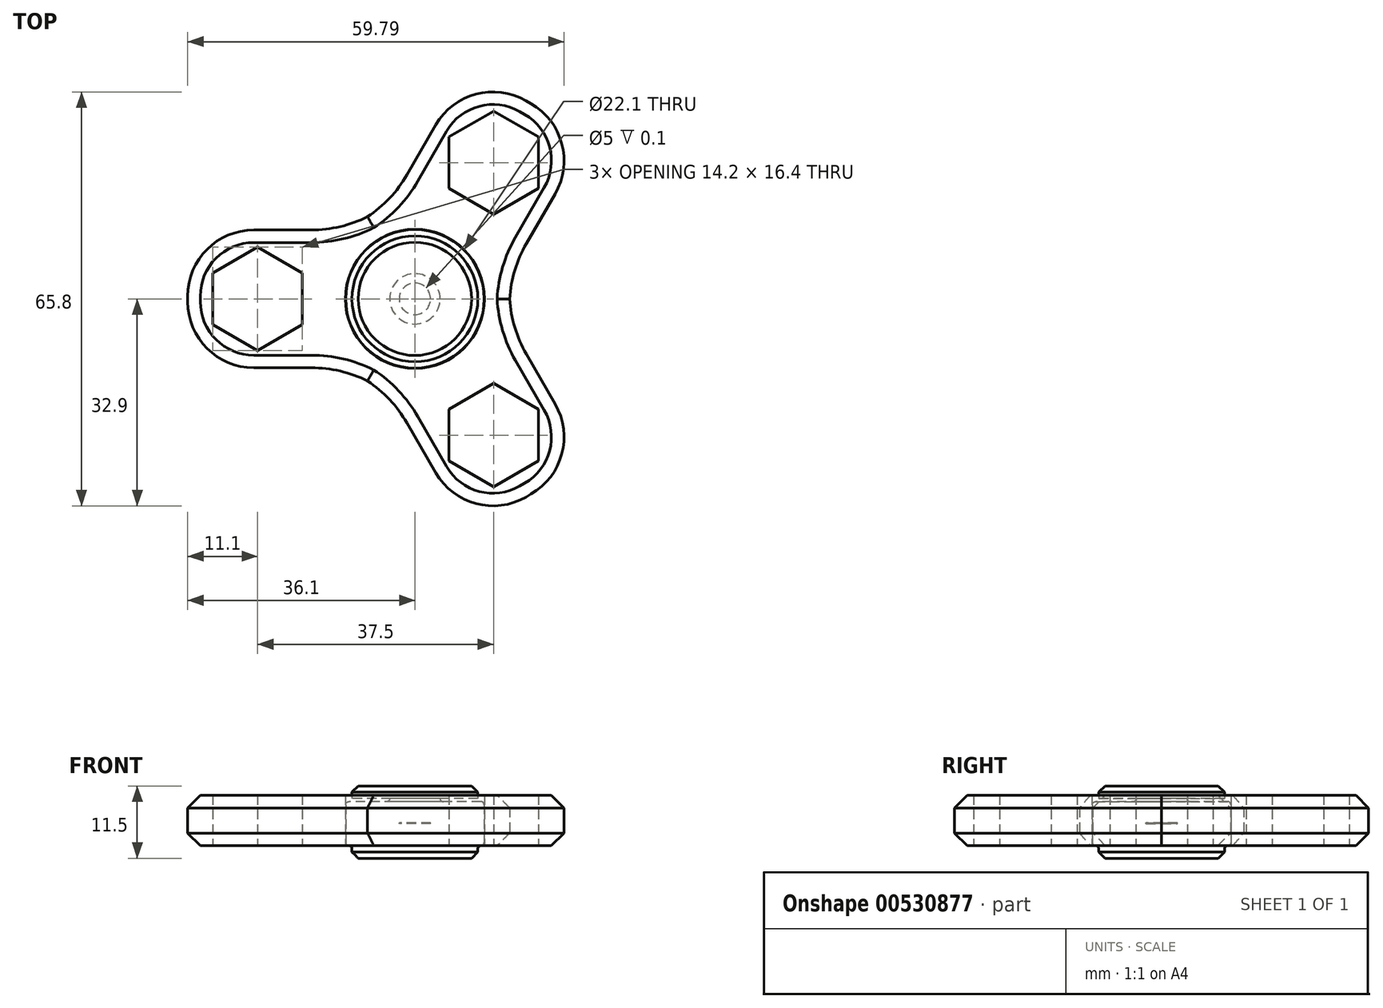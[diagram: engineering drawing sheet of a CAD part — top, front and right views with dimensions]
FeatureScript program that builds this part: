
annotation { "Feature Type Name" : "Feature", "Feature Type Description" : "" }
export const myFeature = defineFeature(function(context is Context, id is Id, definition is map)
    precondition{}
    {
        {
            var Q0;
            Q0=qCreatedBy(makeId("Top.planeOp"),FACE);
            var sketch = newSketch(context, id + "F0", { "sketchPlane" : qUnion([Q0])});
            skCircle(sketch, "E0", {"center": v(0, 0) * mm, "radius": 11 * mm});
            skCircle(sketch, "E1", {"center": v(0, 0) * mm, "radius": 4 * mm});
            skSolve(sketch);
        }
        {
            var Q0;
            Q0=makeQuery(id+"F0.imprint","IMPRINT",FACE,{"disambiguationData":[TD([[makeQuery(id+"F0.imprint","IMPRINT",EDGE,{"derivedFrom":sQuery(id+"F0.wireOp",EDGE,"E0")}),1.0]])]});
            extrude(context, id + "F1", {"entities" : qUnion([Q0]), "depth" : 7 * mm, "offsetDistance" : 25 * mm});
        }
        {
            var Q0;
            Q0=makeQuery(id+"F1.opExtrude","CAP_FACE",FACE,{"disambiguationData":[OSD([sQuery(id+"F0.wireOp",EDGE,"E0"),sQuery(id+"F0.wireOp",EDGE,"E1")])],"isStart":true});
            var sketch = newSketch(context, id + "F2", { "sketchPlane" : qUnion([Q0])});
            skCircle(sketch, "E2.0", {"center": v(0, 0) * mm, "radius": 11.05 * mm});
            skCircle(sketch, "E3.0", {"center": v(0, 0) * mm, "radius": 15.05 * mm});
            skLineSegment(sketch, "E4", {"start": v(0, 0) * mm, "end": v(-25, 0) * mm, "construction": true});
            skPoint(sketch, "E5.middle", {"position": v(-25, 0) * mm});
            skCircle(sketch, "E6", {"center": v(0, 0) * mm, "radius": 50 * mm, "construction": true});
            skCircle(sketch, "E7", {"center": v(-25, 0) * mm, "radius": 8.2 * mm, "construction": true});
            skLineSegment(sketch, "E8.0", {"start": v(-25, -8.2) * mm, "end": v(-32.1, -4.1) * mm});
            skLineSegment(sketch, "E8.1", {"start": v(-32.1, -4.1) * mm, "end": v(-32.1, 4.1) * mm});
            skLineSegment(sketch, "E8.2", {"start": v(-32.1, 4.1) * mm, "end": v(-25, 8.2) * mm});
            skLineSegment(sketch, "E8.3", {"start": v(-25, 8.2) * mm, "end": v(-17.9, 4.1) * mm});
            skLineSegment(sketch, "E8.4", {"start": v(-17.9, 4.1) * mm, "end": v(-17.9, -4.1) * mm});
            skLineSegment(sketch, "E8.5", {"start": v(-17.9, -4.1) * mm, "end": v(-25, -8.2) * mm});
            skLineSegment(sketch, "E9", {"start": v(0, -8.2) * mm, "end": v(-34.67, -8.2) * mm, "construction": true});
            skLineSegment(sketch, "E10", {"start": v(0, 8.2) * mm, "end": v(-34.67, 8.2) * mm, "construction": true});
            skLineSegment(sketch, "E11.0", {"start": v(-1.48, 10.95) * mm, "end": v(-6, 10.95) * mm, "construction": true});
            skLineSegment(sketch, "E12.0", {"start": v(-1.48, -10.95) * mm, "end": v(-6, -10.95) * mm, "construction": true});
            skLineSegment(sketch, "E13", {"start": v(-36.1, -0.45) * mm, "end": v(-36.1, 0.45) * mm});
            skLineSegment(sketch, "E14", {"start": v(-25, 0) * mm, "end": v(-36.1, 0) * mm, "construction": true});
            skPoint(sketch, "E15.visualSharp", {"position": v(-36.1, -10.95) * mm});
            skArc(sketch, "E15.filletArc", {"start": v(-36.1, -0.45) * mm, "mid": v(-33.03, -7.87) * mm, "end": v(-25.6, -10.95) * mm});
            skPoint(sketch, "E16.visualSharp", {"position": v(-36.1, 10.95) * mm});
            skArc(sketch, "E16.filletArc", {"start": v(-25.6, 10.95) * mm, "mid": v(-33.03, 7.87) * mm, "end": v(-36.1, 0.45) * mm});
            skLineSegment(sketch, "E17.trimOffspring", {"start": v(-10.32, -10.95) * mm, "end": v(-25.6, -10.95) * mm});
            skLineSegment(sketch, "E18.trimOffspring", {"start": v(-10.32, 10.95) * mm, "end": v(-25.6, 10.95) * mm});
            skLineSegment(sketch, "E19.1.0", {"start": v(12.5, -13.45) * mm, "end": v(19.6, -17.55) * mm});
            skLineSegment(sketch, "E19.1.1", {"start": v(5.4, -17.55) * mm, "end": v(12.5, -13.45) * mm});
            skLineSegment(sketch, "E19.1.2", {"start": v(5.4, -25.75) * mm, "end": v(5.4, -17.55) * mm});
            skLineSegment(sketch, "E19.1.3", {"start": v(12.5, -29.85) * mm, "end": v(5.4, -25.75) * mm});
            skLineSegment(sketch, "E19.1.4", {"start": v(19.6, -25.75) * mm, "end": v(12.5, -29.85) * mm});
            skLineSegment(sketch, "E19.1.5", {"start": v(19.6, -17.55) * mm, "end": v(19.6, -25.75) * mm});
            skArc(sketch, "E19.1.6", {"start": v(18.44, -31.04) * mm, "mid": v(23.33, -24.66) * mm, "end": v(22.28, -16.7) * mm});
            skLineSegment(sketch, "E19.1.7", {"start": v(14.65, -3.47) * mm, "end": v(22.28, -16.7) * mm});
            skLineSegment(sketch, "E19.1.8", {"start": v(-4.32, -14.42) * mm, "end": v(3.32, -27.65) * mm});
            skArc(sketch, "E19.1.9", {"start": v(3.32, -27.65) * mm, "mid": v(9.7, -32.54) * mm, "end": v(17.66, -31.49) * mm});
            skLineSegment(sketch, "E19.1.10", {"start": v(18.44, -31.04) * mm, "end": v(17.66, -31.49) * mm});
            skLineSegment(sketch, "E19.2.0", {"start": v(5.4, 17.55) * mm, "end": v(5.4, 25.75) * mm});
            skLineSegment(sketch, "E19.2.1", {"start": v(12.5, 13.45) * mm, "end": v(5.4, 17.55) * mm});
            skLineSegment(sketch, "E19.2.2", {"start": v(19.6, 17.55) * mm, "end": v(12.5, 13.45) * mm});
            skLineSegment(sketch, "E19.2.3", {"start": v(19.6, 25.75) * mm, "end": v(19.6, 17.55) * mm});
            skLineSegment(sketch, "E19.2.4", {"start": v(12.5, 29.85) * mm, "end": v(19.6, 25.75) * mm});
            skLineSegment(sketch, "E19.2.5", {"start": v(5.4, 25.75) * mm, "end": v(12.5, 29.85) * mm});
            skArc(sketch, "E19.2.6", {"start": v(17.66, 31.49) * mm, "mid": v(9.7, 32.54) * mm, "end": v(3.32, 27.65) * mm});
            skLineSegment(sketch, "E19.2.7", {"start": v(-4.32, 14.42) * mm, "end": v(3.32, 27.65) * mm});
            skLineSegment(sketch, "E19.2.8", {"start": v(14.65, 3.47) * mm, "end": v(22.28, 16.7) * mm});
            skArc(sketch, "E19.2.9", {"start": v(22.28, 16.7) * mm, "mid": v(23.33, 24.66) * mm, "end": v(18.44, 31.04) * mm});
            skLineSegment(sketch, "E19.2.10", {"start": v(17.66, 31.49) * mm, "end": v(18.44, 31.04) * mm});
            skSolve(sketch);
        }
        {
            var Q0;
            {var subQ5=sQuery(id+"F2.wireOp",EDGE,"2090168d-b076-447e-ab9d-785cbba13f1d.2.0");Q0=makeQuery(id+"F2.imprint","IMPRINT",FACE,{"disambiguationData":[TD([[makeQuery(id+"F2.imprint","IMPRINT",EDGE,{"derivedFrom":subQ5}),-1.0]])]});}
            var Q1;
            Q1=makeQuery(id+"F2.imprint","IMPRINT",FACE,{"disambiguationData":[TD([[makeQuery(id+"F2.imprint","IMPRINT",EDGE,{"derivedFrom":sQuery(id+"F2.wireOp",EDGE,"E2.0")}),-1.0]])]});
            var Q2;
            {var subQ6=sQuery(id+"F2.wireOp",EDGE,"2090168d-b076-447e-ab9d-785cbba13f1d.1.0");Q2=makeQuery(id+"F2.imprint","IMPRINT",FACE,{"disambiguationData":[TD([[makeQuery(id+"F2.imprint","IMPRINT",EDGE,{"derivedFrom":subQ6}),-1.0]])]});}
            var Q3;
            {var subQ5=sQuery(id+"F2.wireOp",EDGE,"E5.bottom");Q3=makeQuery(id+"F2.imprint","IMPRINT",FACE,{"disambiguationData":[TD([[makeQuery(id+"F2.imprint","IMPRINT",EDGE,{"derivedFrom":subQ5}),-1.0]])]});}
            var Q4;
            {var subQ3=sQuery(id+"F2.wireOp",EDGE,"E8.0");Q4=makeQuery(id+"F2.imprint","IMPRINT",FACE,{"disambiguationData":[TD([[makeQuery(id+"F2.imprint","IMPRINT",EDGE,{"derivedFrom":subQ3}),1.0]])]});}
            var Q5;
            {var subQ7=sQuery(id+"F2.wireOp",EDGE,"1de061e3-998c-4d38-ad47-f643a90dabba.1.3");Q5=makeQuery(id+"F2.imprint","IMPRINT",FACE,{"disambiguationData":[TD([[makeQuery(id+"F2.imprint","IMPRINT",EDGE,{"derivedFrom":subQ7}),1.0]])]});}
            var Q6;
            {var subQ5=sQuery(id+"F2.wireOp",EDGE,"1de061e3-998c-4d38-ad47-f643a90dabba.2.3");Q6=makeQuery(id+"F2.imprint","IMPRINT",FACE,{"disambiguationData":[TD([[makeQuery(id+"F2.imprint","IMPRINT",EDGE,{"derivedFrom":subQ5}),1.0]])]});}
            var Q7;
            {var subQ6=sQuery(id+"F2.wireOp",EDGE,"E19.2.3");Q7=makeQuery(id+"F2.imprint","IMPRINT",FACE,{"disambiguationData":[TD([[makeQuery(id+"F2.imprint","IMPRINT",EDGE,{"derivedFrom":subQ6}),1.0]])]});}
            var Q8;
            {var subQ7=sQuery(id+"F2.wireOp",EDGE,"E19.1.3");Q8=makeQuery(id+"F2.imprint","IMPRINT",FACE,{"disambiguationData":[TD([[makeQuery(id+"F2.imprint","IMPRINT",EDGE,{"derivedFrom":subQ7}),1.0]])]});}
            extrude(context, id + "F3", {"entities" : qUnion([Q0, Q1, Q2, Q3, Q4, Q5, Q6, Q7, Q8]), "oppositeDirection" : true, "depth" : 8 * mm, "offsetDistance" : 25 * mm});
        }
        {
            var Q0;
            Q0=makeQuery(id+"F3.opExtrude","SWEPT_EDGE",EDGE,{"disambiguationData":[OSD([sQuery(id+"F2.wireOp",EDGE,"E3.0"),sQuery(id+"F2.wireOp",EDGE,"2090168d-b076-447e-ab9d-785cbba13f1d.2.3")])]});
            var Q1;
            Q1=makeQuery(id+"F3.opExtrude","SWEPT_EDGE",EDGE,{"disambiguationData":[OSD([sQuery(id+"F2.wireOp",EDGE,"E3.0"),sQuery(id+"F2.wireOp",EDGE,"2090168d-b076-447e-ab9d-785cbba13f1d.1.8")])]});
            var Q2;
            Q2=makeQuery(id+"F3.opExtrude","SWEPT_EDGE",EDGE,{"disambiguationData":[OSD([sQuery(id+"F2.wireOp",EDGE,"E3.0"),sQuery(id+"F2.wireOp",EDGE,"2090168d-b076-447e-ab9d-785cbba13f1d.2.8")])]});
            var Q3;
            Q3=makeQuery(id+"F3.opExtrude","SWEPT_EDGE",EDGE,{"disambiguationData":[OSD([sQuery(id+"F2.wireOp",EDGE,"E3.0"),sQuery(id+"F2.wireOp",EDGE,"7743fc66-aecd-449a-ba36-aedd3b808c0c.trimOffspring")])]});
            var Q4;
            Q4=makeQuery(id+"F3.opExtrude","SWEPT_EDGE",EDGE,{"disambiguationData":[OSD([sQuery(id+"F2.wireOp",EDGE,"E3.0"),sQuery(id+"F2.wireOp",EDGE,"1c2b6c41-6d39-4d1e-a6ba-ca666f8f76650.MirrorCS")])]});
            var Q5;
            Q5=makeQuery(id+"F3.opExtrude","SWEPT_EDGE",EDGE,{"disambiguationData":[OSD([sQuery(id+"F2.wireOp",EDGE,"E3.0"),sQuery(id+"F2.wireOp",EDGE,"2090168d-b076-447e-ab9d-785cbba13f1d.1.3")])]});
            fillet(context, id + "F4", {"entities" : qUnion([Q0, Q1, Q2, Q3, Q4, Q5]), "radius" : 20 * mm, "tangentPropagation" : true, "allowEdgeOverflow" : false});
        }
        {
            var Q0;
            Q0=makeQuery(id+"F3.opExtrude","CAP_EDGE",EDGE,{"disambiguationData":[OSD([sQuery(id+"F2.wireOp",EDGE,"E19.2.9")])],"isStart":false});
            var Q1;
            {var subQ0=sQuery(id+"F2.wireOp",EDGE,"E17.trimOffspring");var subQ1=sQuery(id+"F2.wireOp",EDGE,"E3.0");Q1=makeQuery(id+"F4.opFillet","BLEND_EDGE",EDGE,{"blendedFrom":[makeQuery(id+"F3.opExtrude","SWEPT_EDGE",EDGE,{"disambiguationData":[OSD([subQ1,subQ0])]}),makeQuery(id+"F3.opExtrude","CAP_FACE",FACE,{"disambiguationData":[OSD([sQuery(id+"F2.wireOp",EDGE,"E2.0"),subQ1,sQuery(id+"F2.wireOp",EDGE,"E8.0"),sQuery(id+"F2.wireOp",EDGE,"E8.1"),sQuery(id+"F2.wireOp",EDGE,"E8.2"),sQuery(id+"F2.wireOp",EDGE,"E8.3"),sQuery(id+"F2.wireOp",EDGE,"E8.4"),sQuery(id+"F2.wireOp",EDGE,"E8.5"),sQuery(id+"F2.wireOp",EDGE,"E15.filletArc"),sQuery(id+"F2.wireOp",EDGE,"E16.filletArc"),subQ0,sQuery(id+"F2.wireOp",EDGE,"E18.trimOffspring"),sQuery(id+"F2.wireOp",EDGE,"E19.1.0"),sQuery(id+"F2.wireOp",EDGE,"E19.1.1"),sQuery(id+"F2.wireOp",EDGE,"E19.1.2"),sQuery(id+"F2.wireOp",EDGE,"E19.1.3"),sQuery(id+"F2.wireOp",EDGE,"E19.1.4"),sQuery(id+"F2.wireOp",EDGE,"E19.1.5"),sQuery(id+"F2.wireOp",EDGE,"E19.1.6"),sQuery(id+"F2.wireOp",EDGE,"E19.1.7"),sQuery(id+"F2.wireOp",EDGE,"E19.1.8"),sQuery(id+"F2.wireOp",EDGE,"E19.1.9"),sQuery(id+"F2.wireOp",EDGE,"E19.2.0"),sQuery(id+"F2.wireOp",EDGE,"E19.2.1"),sQuery(id+"F2.wireOp",EDGE,"E19.2.2"),sQuery(id+"F2.wireOp",EDGE,"E19.2.3"),sQuery(id+"F2.wireOp",EDGE,"E19.2.4"),sQuery(id+"F2.wireOp",EDGE,"E19.2.5"),sQuery(id+"F2.wireOp",EDGE,"E19.2.6"),sQuery(id+"F2.wireOp",EDGE,"E19.2.7"),sQuery(id+"F2.wireOp",EDGE,"E19.2.8"),sQuery(id+"F2.wireOp",EDGE,"E19.2.9")])],"isStart":false})],"blendedInto":[makeQuery(id+"F3.opExtrude","CAP_FACE",FACE,{"disambiguationData":[OSD([sQuery(id+"F2.wireOp",EDGE,"E2.0"),subQ1,sQuery(id+"F2.wireOp",EDGE,"E8.0"),sQuery(id+"F2.wireOp",EDGE,"E8.1"),sQuery(id+"F2.wireOp",EDGE,"E8.2"),sQuery(id+"F2.wireOp",EDGE,"E8.3"),sQuery(id+"F2.wireOp",EDGE,"E8.4"),sQuery(id+"F2.wireOp",EDGE,"E8.5"),sQuery(id+"F2.wireOp",EDGE,"E15.filletArc"),sQuery(id+"F2.wireOp",EDGE,"E16.filletArc"),subQ0,sQuery(id+"F2.wireOp",EDGE,"E18.trimOffspring"),sQuery(id+"F2.wireOp",EDGE,"E19.1.0"),sQuery(id+"F2.wireOp",EDGE,"E19.1.1"),sQuery(id+"F2.wireOp",EDGE,"E19.1.2"),sQuery(id+"F2.wireOp",EDGE,"E19.1.3"),sQuery(id+"F2.wireOp",EDGE,"E19.1.4"),sQuery(id+"F2.wireOp",EDGE,"E19.1.5"),sQuery(id+"F2.wireOp",EDGE,"E19.1.6"),sQuery(id+"F2.wireOp",EDGE,"E19.1.7"),sQuery(id+"F2.wireOp",EDGE,"E19.1.8"),sQuery(id+"F2.wireOp",EDGE,"E19.1.9"),sQuery(id+"F2.wireOp",EDGE,"E19.2.0"),sQuery(id+"F2.wireOp",EDGE,"E19.2.1"),sQuery(id+"F2.wireOp",EDGE,"E19.2.2"),sQuery(id+"F2.wireOp",EDGE,"E19.2.3"),sQuery(id+"F2.wireOp",EDGE,"E19.2.4"),sQuery(id+"F2.wireOp",EDGE,"E19.2.5"),sQuery(id+"F2.wireOp",EDGE,"E19.2.6"),sQuery(id+"F2.wireOp",EDGE,"E19.2.7"),sQuery(id+"F2.wireOp",EDGE,"E19.2.8"),sQuery(id+"F2.wireOp",EDGE,"E19.2.9")])],"isStart":false})]});}
            var Q2;
            Q2=makeQuery(id+"F3.opExtrude","CAP_EDGE",EDGE,{"disambiguationData":[OSD([sQuery(id+"F2.wireOp",EDGE,"E19.1.6")])],"isStart":false});
            var Q3;
            Q3=makeQuery(id+"F3.opExtrude","CAP_EDGE",EDGE,{"disambiguationData":[OSD([sQuery(id+"F2.wireOp",EDGE,"E18.trimOffspring")])],"isStart":false});
            var Q4;
            {var subQ0=sQuery(id+"F2.wireOp",EDGE,"E18.trimOffspring");var subQ1=sQuery(id+"F2.wireOp",EDGE,"E3.0");Q4=makeQuery(id+"F4.opFillet","BLEND_EDGE",EDGE,{"blendedFrom":[makeQuery(id+"F3.opExtrude","SWEPT_EDGE",EDGE,{"disambiguationData":[OSD([subQ1,subQ0])]}),makeQuery(id+"F3.opExtrude","CAP_FACE",FACE,{"disambiguationData":[OSD([sQuery(id+"F2.wireOp",EDGE,"E2.0"),subQ1,sQuery(id+"F2.wireOp",EDGE,"E8.0"),sQuery(id+"F2.wireOp",EDGE,"E8.1"),sQuery(id+"F2.wireOp",EDGE,"E8.2"),sQuery(id+"F2.wireOp",EDGE,"E8.3"),sQuery(id+"F2.wireOp",EDGE,"E8.4"),sQuery(id+"F2.wireOp",EDGE,"E8.5"),sQuery(id+"F2.wireOp",EDGE,"E15.filletArc"),sQuery(id+"F2.wireOp",EDGE,"E16.filletArc"),sQuery(id+"F2.wireOp",EDGE,"E17.trimOffspring"),subQ0,sQuery(id+"F2.wireOp",EDGE,"E19.1.0"),sQuery(id+"F2.wireOp",EDGE,"E19.1.1"),sQuery(id+"F2.wireOp",EDGE,"E19.1.2"),sQuery(id+"F2.wireOp",EDGE,"E19.1.3"),sQuery(id+"F2.wireOp",EDGE,"E19.1.4"),sQuery(id+"F2.wireOp",EDGE,"E19.1.5"),sQuery(id+"F2.wireOp",EDGE,"E19.1.6"),sQuery(id+"F2.wireOp",EDGE,"E19.1.7"),sQuery(id+"F2.wireOp",EDGE,"E19.1.8"),sQuery(id+"F2.wireOp",EDGE,"E19.1.9"),sQuery(id+"F2.wireOp",EDGE,"E19.2.0"),sQuery(id+"F2.wireOp",EDGE,"E19.2.1"),sQuery(id+"F2.wireOp",EDGE,"E19.2.2"),sQuery(id+"F2.wireOp",EDGE,"E19.2.3"),sQuery(id+"F2.wireOp",EDGE,"E19.2.4"),sQuery(id+"F2.wireOp",EDGE,"E19.2.5"),sQuery(id+"F2.wireOp",EDGE,"E19.2.6"),sQuery(id+"F2.wireOp",EDGE,"E19.2.7"),sQuery(id+"F2.wireOp",EDGE,"E19.2.8"),sQuery(id+"F2.wireOp",EDGE,"E19.2.9")])],"isStart":false})],"blendedInto":[makeQuery(id+"F3.opExtrude","CAP_FACE",FACE,{"disambiguationData":[OSD([sQuery(id+"F2.wireOp",EDGE,"E2.0"),subQ1,sQuery(id+"F2.wireOp",EDGE,"E8.0"),sQuery(id+"F2.wireOp",EDGE,"E8.1"),sQuery(id+"F2.wireOp",EDGE,"E8.2"),sQuery(id+"F2.wireOp",EDGE,"E8.3"),sQuery(id+"F2.wireOp",EDGE,"E8.4"),sQuery(id+"F2.wireOp",EDGE,"E8.5"),sQuery(id+"F2.wireOp",EDGE,"E15.filletArc"),sQuery(id+"F2.wireOp",EDGE,"E16.filletArc"),sQuery(id+"F2.wireOp",EDGE,"E17.trimOffspring"),subQ0,sQuery(id+"F2.wireOp",EDGE,"E19.1.0"),sQuery(id+"F2.wireOp",EDGE,"E19.1.1"),sQuery(id+"F2.wireOp",EDGE,"E19.1.2"),sQuery(id+"F2.wireOp",EDGE,"E19.1.3"),sQuery(id+"F2.wireOp",EDGE,"E19.1.4"),sQuery(id+"F2.wireOp",EDGE,"E19.1.5"),sQuery(id+"F2.wireOp",EDGE,"E19.1.6"),sQuery(id+"F2.wireOp",EDGE,"E19.1.7"),sQuery(id+"F2.wireOp",EDGE,"E19.1.8"),sQuery(id+"F2.wireOp",EDGE,"E19.1.9"),sQuery(id+"F2.wireOp",EDGE,"E19.2.0"),sQuery(id+"F2.wireOp",EDGE,"E19.2.1"),sQuery(id+"F2.wireOp",EDGE,"E19.2.2"),sQuery(id+"F2.wireOp",EDGE,"E19.2.3"),sQuery(id+"F2.wireOp",EDGE,"E19.2.4"),sQuery(id+"F2.wireOp",EDGE,"E19.2.5"),sQuery(id+"F2.wireOp",EDGE,"E19.2.6"),sQuery(id+"F2.wireOp",EDGE,"E19.2.7"),sQuery(id+"F2.wireOp",EDGE,"E19.2.8"),sQuery(id+"F2.wireOp",EDGE,"E19.2.9")])],"isStart":false})]});}
            var Q5;
            {var subQ0=sQuery(id+"F2.wireOp",EDGE,"E19.2.7");var subQ1=sQuery(id+"F2.wireOp",EDGE,"E3.0");Q5=makeQuery(id+"F4.opFillet","BLEND_EDGE",EDGE,{"blendedFrom":[makeQuery(id+"F3.opExtrude","SWEPT_EDGE",EDGE,{"disambiguationData":[OSD([subQ1,subQ0])]}),makeQuery(id+"F3.opExtrude","CAP_FACE",FACE,{"disambiguationData":[OSD([sQuery(id+"F2.wireOp",EDGE,"E2.0"),subQ1,sQuery(id+"F2.wireOp",EDGE,"E8.0"),sQuery(id+"F2.wireOp",EDGE,"E8.1"),sQuery(id+"F2.wireOp",EDGE,"E8.2"),sQuery(id+"F2.wireOp",EDGE,"E8.3"),sQuery(id+"F2.wireOp",EDGE,"E8.4"),sQuery(id+"F2.wireOp",EDGE,"E8.5"),sQuery(id+"F2.wireOp",EDGE,"E15.filletArc"),sQuery(id+"F2.wireOp",EDGE,"E16.filletArc"),sQuery(id+"F2.wireOp",EDGE,"E17.trimOffspring"),sQuery(id+"F2.wireOp",EDGE,"E18.trimOffspring"),sQuery(id+"F2.wireOp",EDGE,"E19.1.0"),sQuery(id+"F2.wireOp",EDGE,"E19.1.1"),sQuery(id+"F2.wireOp",EDGE,"E19.1.2"),sQuery(id+"F2.wireOp",EDGE,"E19.1.3"),sQuery(id+"F2.wireOp",EDGE,"E19.1.4"),sQuery(id+"F2.wireOp",EDGE,"E19.1.5"),sQuery(id+"F2.wireOp",EDGE,"E19.1.6"),sQuery(id+"F2.wireOp",EDGE,"E19.1.7"),sQuery(id+"F2.wireOp",EDGE,"E19.1.8"),sQuery(id+"F2.wireOp",EDGE,"E19.1.9"),sQuery(id+"F2.wireOp",EDGE,"E19.2.0"),sQuery(id+"F2.wireOp",EDGE,"E19.2.1"),sQuery(id+"F2.wireOp",EDGE,"E19.2.2"),sQuery(id+"F2.wireOp",EDGE,"E19.2.3"),sQuery(id+"F2.wireOp",EDGE,"E19.2.4"),sQuery(id+"F2.wireOp",EDGE,"E19.2.5"),sQuery(id+"F2.wireOp",EDGE,"E19.2.6"),subQ0,sQuery(id+"F2.wireOp",EDGE,"E19.2.8"),sQuery(id+"F2.wireOp",EDGE,"E19.2.9")])],"isStart":false})],"blendedInto":[makeQuery(id+"F3.opExtrude","CAP_FACE",FACE,{"disambiguationData":[OSD([sQuery(id+"F2.wireOp",EDGE,"E2.0"),subQ1,sQuery(id+"F2.wireOp",EDGE,"E8.0"),sQuery(id+"F2.wireOp",EDGE,"E8.1"),sQuery(id+"F2.wireOp",EDGE,"E8.2"),sQuery(id+"F2.wireOp",EDGE,"E8.3"),sQuery(id+"F2.wireOp",EDGE,"E8.4"),sQuery(id+"F2.wireOp",EDGE,"E8.5"),sQuery(id+"F2.wireOp",EDGE,"E15.filletArc"),sQuery(id+"F2.wireOp",EDGE,"E16.filletArc"),sQuery(id+"F2.wireOp",EDGE,"E17.trimOffspring"),sQuery(id+"F2.wireOp",EDGE,"E18.trimOffspring"),sQuery(id+"F2.wireOp",EDGE,"E19.1.0"),sQuery(id+"F2.wireOp",EDGE,"E19.1.1"),sQuery(id+"F2.wireOp",EDGE,"E19.1.2"),sQuery(id+"F2.wireOp",EDGE,"E19.1.3"),sQuery(id+"F2.wireOp",EDGE,"E19.1.4"),sQuery(id+"F2.wireOp",EDGE,"E19.1.5"),sQuery(id+"F2.wireOp",EDGE,"E19.1.6"),sQuery(id+"F2.wireOp",EDGE,"E19.1.7"),sQuery(id+"F2.wireOp",EDGE,"E19.1.8"),sQuery(id+"F2.wireOp",EDGE,"E19.1.9"),sQuery(id+"F2.wireOp",EDGE,"E19.2.0"),sQuery(id+"F2.wireOp",EDGE,"E19.2.1"),sQuery(id+"F2.wireOp",EDGE,"E19.2.2"),sQuery(id+"F2.wireOp",EDGE,"E19.2.3"),sQuery(id+"F2.wireOp",EDGE,"E19.2.4"),sQuery(id+"F2.wireOp",EDGE,"E19.2.5"),sQuery(id+"F2.wireOp",EDGE,"E19.2.6"),subQ0,sQuery(id+"F2.wireOp",EDGE,"E19.2.8"),sQuery(id+"F2.wireOp",EDGE,"E19.2.9")])],"isStart":false})]});}
            var Q6;
            Q6=makeQuery(id+"F3.opExtrude","CAP_EDGE",EDGE,{"disambiguationData":[OSD([sQuery(id+"F2.wireOp",EDGE,"E19.2.7")])],"isStart":false});
            var Q7;
            Q7=makeQuery(id+"F3.opExtrude","CAP_EDGE",EDGE,{"disambiguationData":[OSD([sQuery(id+"F2.wireOp",EDGE,"E19.2.6")])],"isStart":false});
            var Q8;
            {var subQ0=sQuery(id+"F2.wireOp",EDGE,"E19.2.8");var subQ1=sQuery(id+"F2.wireOp",EDGE,"E3.0");Q8=makeQuery(id+"F4.opFillet","BLEND_EDGE",EDGE,{"blendedFrom":[makeQuery(id+"F3.opExtrude","SWEPT_EDGE",EDGE,{"disambiguationData":[OSD([subQ1,subQ0])]}),makeQuery(id+"F3.opExtrude","CAP_FACE",FACE,{"disambiguationData":[OSD([sQuery(id+"F2.wireOp",EDGE,"E2.0"),subQ1,sQuery(id+"F2.wireOp",EDGE,"E8.0"),sQuery(id+"F2.wireOp",EDGE,"E8.1"),sQuery(id+"F2.wireOp",EDGE,"E8.2"),sQuery(id+"F2.wireOp",EDGE,"E8.3"),sQuery(id+"F2.wireOp",EDGE,"E8.4"),sQuery(id+"F2.wireOp",EDGE,"E8.5"),sQuery(id+"F2.wireOp",EDGE,"E15.filletArc"),sQuery(id+"F2.wireOp",EDGE,"E16.filletArc"),sQuery(id+"F2.wireOp",EDGE,"E17.trimOffspring"),sQuery(id+"F2.wireOp",EDGE,"E18.trimOffspring"),sQuery(id+"F2.wireOp",EDGE,"E19.1.0"),sQuery(id+"F2.wireOp",EDGE,"E19.1.1"),sQuery(id+"F2.wireOp",EDGE,"E19.1.2"),sQuery(id+"F2.wireOp",EDGE,"E19.1.3"),sQuery(id+"F2.wireOp",EDGE,"E19.1.4"),sQuery(id+"F2.wireOp",EDGE,"E19.1.5"),sQuery(id+"F2.wireOp",EDGE,"E19.1.6"),sQuery(id+"F2.wireOp",EDGE,"E19.1.7"),sQuery(id+"F2.wireOp",EDGE,"E19.1.8"),sQuery(id+"F2.wireOp",EDGE,"E19.1.9"),sQuery(id+"F2.wireOp",EDGE,"E19.2.0"),sQuery(id+"F2.wireOp",EDGE,"E19.2.1"),sQuery(id+"F2.wireOp",EDGE,"E19.2.2"),sQuery(id+"F2.wireOp",EDGE,"E19.2.3"),sQuery(id+"F2.wireOp",EDGE,"E19.2.4"),sQuery(id+"F2.wireOp",EDGE,"E19.2.5"),sQuery(id+"F2.wireOp",EDGE,"E19.2.6"),sQuery(id+"F2.wireOp",EDGE,"E19.2.7"),subQ0,sQuery(id+"F2.wireOp",EDGE,"E19.2.9")])],"isStart":false})],"blendedInto":[makeQuery(id+"F3.opExtrude","CAP_FACE",FACE,{"disambiguationData":[OSD([sQuery(id+"F2.wireOp",EDGE,"E2.0"),subQ1,sQuery(id+"F2.wireOp",EDGE,"E8.0"),sQuery(id+"F2.wireOp",EDGE,"E8.1"),sQuery(id+"F2.wireOp",EDGE,"E8.2"),sQuery(id+"F2.wireOp",EDGE,"E8.3"),sQuery(id+"F2.wireOp",EDGE,"E8.4"),sQuery(id+"F2.wireOp",EDGE,"E8.5"),sQuery(id+"F2.wireOp",EDGE,"E15.filletArc"),sQuery(id+"F2.wireOp",EDGE,"E16.filletArc"),sQuery(id+"F2.wireOp",EDGE,"E17.trimOffspring"),sQuery(id+"F2.wireOp",EDGE,"E18.trimOffspring"),sQuery(id+"F2.wireOp",EDGE,"E19.1.0"),sQuery(id+"F2.wireOp",EDGE,"E19.1.1"),sQuery(id+"F2.wireOp",EDGE,"E19.1.2"),sQuery(id+"F2.wireOp",EDGE,"E19.1.3"),sQuery(id+"F2.wireOp",EDGE,"E19.1.4"),sQuery(id+"F2.wireOp",EDGE,"E19.1.5"),sQuery(id+"F2.wireOp",EDGE,"E19.1.6"),sQuery(id+"F2.wireOp",EDGE,"E19.1.7"),sQuery(id+"F2.wireOp",EDGE,"E19.1.8"),sQuery(id+"F2.wireOp",EDGE,"E19.1.9"),sQuery(id+"F2.wireOp",EDGE,"E19.2.0"),sQuery(id+"F2.wireOp",EDGE,"E19.2.1"),sQuery(id+"F2.wireOp",EDGE,"E19.2.2"),sQuery(id+"F2.wireOp",EDGE,"E19.2.3"),sQuery(id+"F2.wireOp",EDGE,"E19.2.4"),sQuery(id+"F2.wireOp",EDGE,"E19.2.5"),sQuery(id+"F2.wireOp",EDGE,"E19.2.6"),sQuery(id+"F2.wireOp",EDGE,"E19.2.7"),subQ0,sQuery(id+"F2.wireOp",EDGE,"E19.2.9")])],"isStart":false})]});}
            var Q9;
            Q9=makeQuery(id+"F3.opExtrude","CAP_EDGE",EDGE,{"disambiguationData":[OSD([sQuery(id+"F2.wireOp",EDGE,"E19.2.8")])],"isStart":false});
            var Q10;
            {var subQ0=sQuery(id+"F2.wireOp",EDGE,"E19.1.7");var subQ1=sQuery(id+"F2.wireOp",EDGE,"E3.0");Q10=makeQuery(id+"F4.opFillet","BLEND_EDGE",EDGE,{"blendedFrom":[makeQuery(id+"F3.opExtrude","SWEPT_EDGE",EDGE,{"disambiguationData":[OSD([subQ1,subQ0])]}),makeQuery(id+"F3.opExtrude","CAP_FACE",FACE,{"disambiguationData":[OSD([sQuery(id+"F2.wireOp",EDGE,"E2.0"),subQ1,sQuery(id+"F2.wireOp",EDGE,"E8.0"),sQuery(id+"F2.wireOp",EDGE,"E8.1"),sQuery(id+"F2.wireOp",EDGE,"E8.2"),sQuery(id+"F2.wireOp",EDGE,"E8.3"),sQuery(id+"F2.wireOp",EDGE,"E8.4"),sQuery(id+"F2.wireOp",EDGE,"E8.5"),sQuery(id+"F2.wireOp",EDGE,"E15.filletArc"),sQuery(id+"F2.wireOp",EDGE,"E16.filletArc"),sQuery(id+"F2.wireOp",EDGE,"E17.trimOffspring"),sQuery(id+"F2.wireOp",EDGE,"E18.trimOffspring"),sQuery(id+"F2.wireOp",EDGE,"E19.1.0"),sQuery(id+"F2.wireOp",EDGE,"E19.1.1"),sQuery(id+"F2.wireOp",EDGE,"E19.1.2"),sQuery(id+"F2.wireOp",EDGE,"E19.1.3"),sQuery(id+"F2.wireOp",EDGE,"E19.1.4"),sQuery(id+"F2.wireOp",EDGE,"E19.1.5"),sQuery(id+"F2.wireOp",EDGE,"E19.1.6"),subQ0,sQuery(id+"F2.wireOp",EDGE,"E19.1.8"),sQuery(id+"F2.wireOp",EDGE,"E19.1.9"),sQuery(id+"F2.wireOp",EDGE,"E19.2.0"),sQuery(id+"F2.wireOp",EDGE,"E19.2.1"),sQuery(id+"F2.wireOp",EDGE,"E19.2.2"),sQuery(id+"F2.wireOp",EDGE,"E19.2.3"),sQuery(id+"F2.wireOp",EDGE,"E19.2.4"),sQuery(id+"F2.wireOp",EDGE,"E19.2.5"),sQuery(id+"F2.wireOp",EDGE,"E19.2.6"),sQuery(id+"F2.wireOp",EDGE,"E19.2.7"),sQuery(id+"F2.wireOp",EDGE,"E19.2.8"),sQuery(id+"F2.wireOp",EDGE,"E19.2.9")])],"isStart":false})],"blendedInto":[makeQuery(id+"F3.opExtrude","CAP_FACE",FACE,{"disambiguationData":[OSD([sQuery(id+"F2.wireOp",EDGE,"E2.0"),subQ1,sQuery(id+"F2.wireOp",EDGE,"E8.0"),sQuery(id+"F2.wireOp",EDGE,"E8.1"),sQuery(id+"F2.wireOp",EDGE,"E8.2"),sQuery(id+"F2.wireOp",EDGE,"E8.3"),sQuery(id+"F2.wireOp",EDGE,"E8.4"),sQuery(id+"F2.wireOp",EDGE,"E8.5"),sQuery(id+"F2.wireOp",EDGE,"E15.filletArc"),sQuery(id+"F2.wireOp",EDGE,"E16.filletArc"),sQuery(id+"F2.wireOp",EDGE,"E17.trimOffspring"),sQuery(id+"F2.wireOp",EDGE,"E18.trimOffspring"),sQuery(id+"F2.wireOp",EDGE,"E19.1.0"),sQuery(id+"F2.wireOp",EDGE,"E19.1.1"),sQuery(id+"F2.wireOp",EDGE,"E19.1.2"),sQuery(id+"F2.wireOp",EDGE,"E19.1.3"),sQuery(id+"F2.wireOp",EDGE,"E19.1.4"),sQuery(id+"F2.wireOp",EDGE,"E19.1.5"),sQuery(id+"F2.wireOp",EDGE,"E19.1.6"),subQ0,sQuery(id+"F2.wireOp",EDGE,"E19.1.8"),sQuery(id+"F2.wireOp",EDGE,"E19.1.9"),sQuery(id+"F2.wireOp",EDGE,"E19.2.0"),sQuery(id+"F2.wireOp",EDGE,"E19.2.1"),sQuery(id+"F2.wireOp",EDGE,"E19.2.2"),sQuery(id+"F2.wireOp",EDGE,"E19.2.3"),sQuery(id+"F2.wireOp",EDGE,"E19.2.4"),sQuery(id+"F2.wireOp",EDGE,"E19.2.5"),sQuery(id+"F2.wireOp",EDGE,"E19.2.6"),sQuery(id+"F2.wireOp",EDGE,"E19.2.7"),sQuery(id+"F2.wireOp",EDGE,"E19.2.8"),sQuery(id+"F2.wireOp",EDGE,"E19.2.9")])],"isStart":false})]});}
            var Q11;
            Q11=makeQuery(id+"F3.opExtrude","CAP_EDGE",EDGE,{"disambiguationData":[OSD([sQuery(id+"F2.wireOp",EDGE,"E19.1.7")])],"isStart":false});
            var Q12;
            Q12=makeQuery(id+"F3.opExtrude","CAP_EDGE",EDGE,{"disambiguationData":[OSD([sQuery(id+"F2.wireOp",EDGE,"E19.1.9")])],"isStart":false});
            var Q13;
            {var subQ0=sQuery(id+"F2.wireOp",EDGE,"E19.1.8");var subQ1=sQuery(id+"F2.wireOp",EDGE,"E3.0");Q13=makeQuery(id+"F4.opFillet","BLEND_EDGE",EDGE,{"blendedFrom":[makeQuery(id+"F3.opExtrude","SWEPT_EDGE",EDGE,{"disambiguationData":[OSD([subQ1,subQ0])]}),makeQuery(id+"F3.opExtrude","CAP_FACE",FACE,{"disambiguationData":[OSD([sQuery(id+"F2.wireOp",EDGE,"E2.0"),subQ1,sQuery(id+"F2.wireOp",EDGE,"E8.0"),sQuery(id+"F2.wireOp",EDGE,"E8.1"),sQuery(id+"F2.wireOp",EDGE,"E8.2"),sQuery(id+"F2.wireOp",EDGE,"E8.3"),sQuery(id+"F2.wireOp",EDGE,"E8.4"),sQuery(id+"F2.wireOp",EDGE,"E8.5"),sQuery(id+"F2.wireOp",EDGE,"E15.filletArc"),sQuery(id+"F2.wireOp",EDGE,"E16.filletArc"),sQuery(id+"F2.wireOp",EDGE,"E17.trimOffspring"),sQuery(id+"F2.wireOp",EDGE,"E18.trimOffspring"),sQuery(id+"F2.wireOp",EDGE,"E19.1.0"),sQuery(id+"F2.wireOp",EDGE,"E19.1.1"),sQuery(id+"F2.wireOp",EDGE,"E19.1.2"),sQuery(id+"F2.wireOp",EDGE,"E19.1.3"),sQuery(id+"F2.wireOp",EDGE,"E19.1.4"),sQuery(id+"F2.wireOp",EDGE,"E19.1.5"),sQuery(id+"F2.wireOp",EDGE,"E19.1.6"),sQuery(id+"F2.wireOp",EDGE,"E19.1.7"),subQ0,sQuery(id+"F2.wireOp",EDGE,"E19.1.9"),sQuery(id+"F2.wireOp",EDGE,"E19.2.0"),sQuery(id+"F2.wireOp",EDGE,"E19.2.1"),sQuery(id+"F2.wireOp",EDGE,"E19.2.2"),sQuery(id+"F2.wireOp",EDGE,"E19.2.3"),sQuery(id+"F2.wireOp",EDGE,"E19.2.4"),sQuery(id+"F2.wireOp",EDGE,"E19.2.5"),sQuery(id+"F2.wireOp",EDGE,"E19.2.6"),sQuery(id+"F2.wireOp",EDGE,"E19.2.7"),sQuery(id+"F2.wireOp",EDGE,"E19.2.8"),sQuery(id+"F2.wireOp",EDGE,"E19.2.9")])],"isStart":true})],"blendedInto":[makeQuery(id+"F3.opExtrude","CAP_FACE",FACE,{"disambiguationData":[OSD([sQuery(id+"F2.wireOp",EDGE,"E2.0"),subQ1,sQuery(id+"F2.wireOp",EDGE,"E8.0"),sQuery(id+"F2.wireOp",EDGE,"E8.1"),sQuery(id+"F2.wireOp",EDGE,"E8.2"),sQuery(id+"F2.wireOp",EDGE,"E8.3"),sQuery(id+"F2.wireOp",EDGE,"E8.4"),sQuery(id+"F2.wireOp",EDGE,"E8.5"),sQuery(id+"F2.wireOp",EDGE,"E15.filletArc"),sQuery(id+"F2.wireOp",EDGE,"E16.filletArc"),sQuery(id+"F2.wireOp",EDGE,"E17.trimOffspring"),sQuery(id+"F2.wireOp",EDGE,"E18.trimOffspring"),sQuery(id+"F2.wireOp",EDGE,"E19.1.0"),sQuery(id+"F2.wireOp",EDGE,"E19.1.1"),sQuery(id+"F2.wireOp",EDGE,"E19.1.2"),sQuery(id+"F2.wireOp",EDGE,"E19.1.3"),sQuery(id+"F2.wireOp",EDGE,"E19.1.4"),sQuery(id+"F2.wireOp",EDGE,"E19.1.5"),sQuery(id+"F2.wireOp",EDGE,"E19.1.6"),sQuery(id+"F2.wireOp",EDGE,"E19.1.7"),subQ0,sQuery(id+"F2.wireOp",EDGE,"E19.1.9"),sQuery(id+"F2.wireOp",EDGE,"E19.2.0"),sQuery(id+"F2.wireOp",EDGE,"E19.2.1"),sQuery(id+"F2.wireOp",EDGE,"E19.2.2"),sQuery(id+"F2.wireOp",EDGE,"E19.2.3"),sQuery(id+"F2.wireOp",EDGE,"E19.2.4"),sQuery(id+"F2.wireOp",EDGE,"E19.2.5"),sQuery(id+"F2.wireOp",EDGE,"E19.2.6"),sQuery(id+"F2.wireOp",EDGE,"E19.2.7"),sQuery(id+"F2.wireOp",EDGE,"E19.2.8"),sQuery(id+"F2.wireOp",EDGE,"E19.2.9")])],"isStart":true})]});}
            var Q14;
            Q14=makeQuery(id+"F3.opExtrude","CAP_EDGE",EDGE,{"disambiguationData":[OSD([sQuery(id+"F2.wireOp",EDGE,"E19.1.9")])],"isStart":true});
            var Q15;
            Q15=makeQuery(id+"F3.opExtrude","CAP_EDGE",EDGE,{"disambiguationData":[OSD([sQuery(id+"F2.wireOp",EDGE,"E19.1.6")])],"isStart":true});
            var Q16;
            {var subQ0=sQuery(id+"F2.wireOp",EDGE,"E19.1.7");var subQ1=sQuery(id+"F2.wireOp",EDGE,"E3.0");Q16=makeQuery(id+"F4.opFillet","BLEND_EDGE",EDGE,{"blendedFrom":[makeQuery(id+"F3.opExtrude","SWEPT_EDGE",EDGE,{"disambiguationData":[OSD([subQ1,subQ0])]}),makeQuery(id+"F3.opExtrude","CAP_FACE",FACE,{"disambiguationData":[OSD([sQuery(id+"F2.wireOp",EDGE,"E2.0"),subQ1,sQuery(id+"F2.wireOp",EDGE,"E8.0"),sQuery(id+"F2.wireOp",EDGE,"E8.1"),sQuery(id+"F2.wireOp",EDGE,"E8.2"),sQuery(id+"F2.wireOp",EDGE,"E8.3"),sQuery(id+"F2.wireOp",EDGE,"E8.4"),sQuery(id+"F2.wireOp",EDGE,"E8.5"),sQuery(id+"F2.wireOp",EDGE,"E15.filletArc"),sQuery(id+"F2.wireOp",EDGE,"E16.filletArc"),sQuery(id+"F2.wireOp",EDGE,"E17.trimOffspring"),sQuery(id+"F2.wireOp",EDGE,"E18.trimOffspring"),sQuery(id+"F2.wireOp",EDGE,"E19.1.0"),sQuery(id+"F2.wireOp",EDGE,"E19.1.1"),sQuery(id+"F2.wireOp",EDGE,"E19.1.2"),sQuery(id+"F2.wireOp",EDGE,"E19.1.3"),sQuery(id+"F2.wireOp",EDGE,"E19.1.4"),sQuery(id+"F2.wireOp",EDGE,"E19.1.5"),sQuery(id+"F2.wireOp",EDGE,"E19.1.6"),subQ0,sQuery(id+"F2.wireOp",EDGE,"E19.1.8"),sQuery(id+"F2.wireOp",EDGE,"E19.1.9"),sQuery(id+"F2.wireOp",EDGE,"E19.2.0"),sQuery(id+"F2.wireOp",EDGE,"E19.2.1"),sQuery(id+"F2.wireOp",EDGE,"E19.2.2"),sQuery(id+"F2.wireOp",EDGE,"E19.2.3"),sQuery(id+"F2.wireOp",EDGE,"E19.2.4"),sQuery(id+"F2.wireOp",EDGE,"E19.2.5"),sQuery(id+"F2.wireOp",EDGE,"E19.2.6"),sQuery(id+"F2.wireOp",EDGE,"E19.2.7"),sQuery(id+"F2.wireOp",EDGE,"E19.2.8"),sQuery(id+"F2.wireOp",EDGE,"E19.2.9")])],"isStart":true})],"blendedInto":[makeQuery(id+"F3.opExtrude","CAP_FACE",FACE,{"disambiguationData":[OSD([sQuery(id+"F2.wireOp",EDGE,"E2.0"),subQ1,sQuery(id+"F2.wireOp",EDGE,"E8.0"),sQuery(id+"F2.wireOp",EDGE,"E8.1"),sQuery(id+"F2.wireOp",EDGE,"E8.2"),sQuery(id+"F2.wireOp",EDGE,"E8.3"),sQuery(id+"F2.wireOp",EDGE,"E8.4"),sQuery(id+"F2.wireOp",EDGE,"E8.5"),sQuery(id+"F2.wireOp",EDGE,"E15.filletArc"),sQuery(id+"F2.wireOp",EDGE,"E16.filletArc"),sQuery(id+"F2.wireOp",EDGE,"E17.trimOffspring"),sQuery(id+"F2.wireOp",EDGE,"E18.trimOffspring"),sQuery(id+"F2.wireOp",EDGE,"E19.1.0"),sQuery(id+"F2.wireOp",EDGE,"E19.1.1"),sQuery(id+"F2.wireOp",EDGE,"E19.1.2"),sQuery(id+"F2.wireOp",EDGE,"E19.1.3"),sQuery(id+"F2.wireOp",EDGE,"E19.1.4"),sQuery(id+"F2.wireOp",EDGE,"E19.1.5"),sQuery(id+"F2.wireOp",EDGE,"E19.1.6"),subQ0,sQuery(id+"F2.wireOp",EDGE,"E19.1.8"),sQuery(id+"F2.wireOp",EDGE,"E19.1.9"),sQuery(id+"F2.wireOp",EDGE,"E19.2.0"),sQuery(id+"F2.wireOp",EDGE,"E19.2.1"),sQuery(id+"F2.wireOp",EDGE,"E19.2.2"),sQuery(id+"F2.wireOp",EDGE,"E19.2.3"),sQuery(id+"F2.wireOp",EDGE,"E19.2.4"),sQuery(id+"F2.wireOp",EDGE,"E19.2.5"),sQuery(id+"F2.wireOp",EDGE,"E19.2.6"),sQuery(id+"F2.wireOp",EDGE,"E19.2.7"),sQuery(id+"F2.wireOp",EDGE,"E19.2.8"),sQuery(id+"F2.wireOp",EDGE,"E19.2.9")])],"isStart":true})]});}
            var Q17;
            {var subQ0=sQuery(id+"F2.wireOp",EDGE,"E19.2.7");var subQ1=sQuery(id+"F2.wireOp",EDGE,"E3.0");Q17=makeQuery(id+"F4.opFillet","BLEND_EDGE",EDGE,{"blendedFrom":[makeQuery(id+"F3.opExtrude","SWEPT_EDGE",EDGE,{"disambiguationData":[OSD([subQ1,subQ0])]}),makeQuery(id+"F3.opExtrude","CAP_FACE",FACE,{"disambiguationData":[OSD([sQuery(id+"F2.wireOp",EDGE,"E2.0"),subQ1,sQuery(id+"F2.wireOp",EDGE,"E8.0"),sQuery(id+"F2.wireOp",EDGE,"E8.1"),sQuery(id+"F2.wireOp",EDGE,"E8.2"),sQuery(id+"F2.wireOp",EDGE,"E8.3"),sQuery(id+"F2.wireOp",EDGE,"E8.4"),sQuery(id+"F2.wireOp",EDGE,"E8.5"),sQuery(id+"F2.wireOp",EDGE,"E15.filletArc"),sQuery(id+"F2.wireOp",EDGE,"E16.filletArc"),sQuery(id+"F2.wireOp",EDGE,"E17.trimOffspring"),sQuery(id+"F2.wireOp",EDGE,"E18.trimOffspring"),sQuery(id+"F2.wireOp",EDGE,"E19.1.0"),sQuery(id+"F2.wireOp",EDGE,"E19.1.1"),sQuery(id+"F2.wireOp",EDGE,"E19.1.2"),sQuery(id+"F2.wireOp",EDGE,"E19.1.3"),sQuery(id+"F2.wireOp",EDGE,"E19.1.4"),sQuery(id+"F2.wireOp",EDGE,"E19.1.5"),sQuery(id+"F2.wireOp",EDGE,"E19.1.6"),sQuery(id+"F2.wireOp",EDGE,"E19.1.7"),sQuery(id+"F2.wireOp",EDGE,"E19.1.8"),sQuery(id+"F2.wireOp",EDGE,"E19.1.9"),sQuery(id+"F2.wireOp",EDGE,"E19.2.0"),sQuery(id+"F2.wireOp",EDGE,"E19.2.1"),sQuery(id+"F2.wireOp",EDGE,"E19.2.2"),sQuery(id+"F2.wireOp",EDGE,"E19.2.3"),sQuery(id+"F2.wireOp",EDGE,"E19.2.4"),sQuery(id+"F2.wireOp",EDGE,"E19.2.5"),sQuery(id+"F2.wireOp",EDGE,"E19.2.6"),subQ0,sQuery(id+"F2.wireOp",EDGE,"E19.2.8"),sQuery(id+"F2.wireOp",EDGE,"E19.2.9")])],"isStart":true})],"blendedInto":[makeQuery(id+"F3.opExtrude","CAP_FACE",FACE,{"disambiguationData":[OSD([sQuery(id+"F2.wireOp",EDGE,"E2.0"),subQ1,sQuery(id+"F2.wireOp",EDGE,"E8.0"),sQuery(id+"F2.wireOp",EDGE,"E8.1"),sQuery(id+"F2.wireOp",EDGE,"E8.2"),sQuery(id+"F2.wireOp",EDGE,"E8.3"),sQuery(id+"F2.wireOp",EDGE,"E8.4"),sQuery(id+"F2.wireOp",EDGE,"E8.5"),sQuery(id+"F2.wireOp",EDGE,"E15.filletArc"),sQuery(id+"F2.wireOp",EDGE,"E16.filletArc"),sQuery(id+"F2.wireOp",EDGE,"E17.trimOffspring"),sQuery(id+"F2.wireOp",EDGE,"E18.trimOffspring"),sQuery(id+"F2.wireOp",EDGE,"E19.1.0"),sQuery(id+"F2.wireOp",EDGE,"E19.1.1"),sQuery(id+"F2.wireOp",EDGE,"E19.1.2"),sQuery(id+"F2.wireOp",EDGE,"E19.1.3"),sQuery(id+"F2.wireOp",EDGE,"E19.1.4"),sQuery(id+"F2.wireOp",EDGE,"E19.1.5"),sQuery(id+"F2.wireOp",EDGE,"E19.1.6"),sQuery(id+"F2.wireOp",EDGE,"E19.1.7"),sQuery(id+"F2.wireOp",EDGE,"E19.1.8"),sQuery(id+"F2.wireOp",EDGE,"E19.1.9"),sQuery(id+"F2.wireOp",EDGE,"E19.2.0"),sQuery(id+"F2.wireOp",EDGE,"E19.2.1"),sQuery(id+"F2.wireOp",EDGE,"E19.2.2"),sQuery(id+"F2.wireOp",EDGE,"E19.2.3"),sQuery(id+"F2.wireOp",EDGE,"E19.2.4"),sQuery(id+"F2.wireOp",EDGE,"E19.2.5"),sQuery(id+"F2.wireOp",EDGE,"E19.2.6"),subQ0,sQuery(id+"F2.wireOp",EDGE,"E19.2.8"),sQuery(id+"F2.wireOp",EDGE,"E19.2.9")])],"isStart":true})]});}
            var Q18;
            {var subQ0=sQuery(id+"F2.wireOp",EDGE,"E18.trimOffspring");var subQ1=sQuery(id+"F2.wireOp",EDGE,"E3.0");Q18=makeQuery(id+"F4.opFillet","BLEND_EDGE",EDGE,{"blendedFrom":[makeQuery(id+"F3.opExtrude","SWEPT_EDGE",EDGE,{"disambiguationData":[OSD([subQ1,subQ0])]}),makeQuery(id+"F3.opExtrude","CAP_FACE",FACE,{"disambiguationData":[OSD([sQuery(id+"F2.wireOp",EDGE,"E2.0"),subQ1,sQuery(id+"F2.wireOp",EDGE,"E8.0"),sQuery(id+"F2.wireOp",EDGE,"E8.1"),sQuery(id+"F2.wireOp",EDGE,"E8.2"),sQuery(id+"F2.wireOp",EDGE,"E8.3"),sQuery(id+"F2.wireOp",EDGE,"E8.4"),sQuery(id+"F2.wireOp",EDGE,"E8.5"),sQuery(id+"F2.wireOp",EDGE,"E15.filletArc"),sQuery(id+"F2.wireOp",EDGE,"E16.filletArc"),sQuery(id+"F2.wireOp",EDGE,"E17.trimOffspring"),subQ0,sQuery(id+"F2.wireOp",EDGE,"E19.1.0"),sQuery(id+"F2.wireOp",EDGE,"E19.1.1"),sQuery(id+"F2.wireOp",EDGE,"E19.1.2"),sQuery(id+"F2.wireOp",EDGE,"E19.1.3"),sQuery(id+"F2.wireOp",EDGE,"E19.1.4"),sQuery(id+"F2.wireOp",EDGE,"E19.1.5"),sQuery(id+"F2.wireOp",EDGE,"E19.1.6"),sQuery(id+"F2.wireOp",EDGE,"E19.1.7"),sQuery(id+"F2.wireOp",EDGE,"E19.1.8"),sQuery(id+"F2.wireOp",EDGE,"E19.1.9"),sQuery(id+"F2.wireOp",EDGE,"E19.2.0"),sQuery(id+"F2.wireOp",EDGE,"E19.2.1"),sQuery(id+"F2.wireOp",EDGE,"E19.2.2"),sQuery(id+"F2.wireOp",EDGE,"E19.2.3"),sQuery(id+"F2.wireOp",EDGE,"E19.2.4"),sQuery(id+"F2.wireOp",EDGE,"E19.2.5"),sQuery(id+"F2.wireOp",EDGE,"E19.2.6"),sQuery(id+"F2.wireOp",EDGE,"E19.2.7"),sQuery(id+"F2.wireOp",EDGE,"E19.2.8"),sQuery(id+"F2.wireOp",EDGE,"E19.2.9")])],"isStart":true})],"blendedInto":[makeQuery(id+"F3.opExtrude","CAP_FACE",FACE,{"disambiguationData":[OSD([sQuery(id+"F2.wireOp",EDGE,"E2.0"),subQ1,sQuery(id+"F2.wireOp",EDGE,"E8.0"),sQuery(id+"F2.wireOp",EDGE,"E8.1"),sQuery(id+"F2.wireOp",EDGE,"E8.2"),sQuery(id+"F2.wireOp",EDGE,"E8.3"),sQuery(id+"F2.wireOp",EDGE,"E8.4"),sQuery(id+"F2.wireOp",EDGE,"E8.5"),sQuery(id+"F2.wireOp",EDGE,"E15.filletArc"),sQuery(id+"F2.wireOp",EDGE,"E16.filletArc"),sQuery(id+"F2.wireOp",EDGE,"E17.trimOffspring"),subQ0,sQuery(id+"F2.wireOp",EDGE,"E19.1.0"),sQuery(id+"F2.wireOp",EDGE,"E19.1.1"),sQuery(id+"F2.wireOp",EDGE,"E19.1.2"),sQuery(id+"F2.wireOp",EDGE,"E19.1.3"),sQuery(id+"F2.wireOp",EDGE,"E19.1.4"),sQuery(id+"F2.wireOp",EDGE,"E19.1.5"),sQuery(id+"F2.wireOp",EDGE,"E19.1.6"),sQuery(id+"F2.wireOp",EDGE,"E19.1.7"),sQuery(id+"F2.wireOp",EDGE,"E19.1.8"),sQuery(id+"F2.wireOp",EDGE,"E19.1.9"),sQuery(id+"F2.wireOp",EDGE,"E19.2.0"),sQuery(id+"F2.wireOp",EDGE,"E19.2.1"),sQuery(id+"F2.wireOp",EDGE,"E19.2.2"),sQuery(id+"F2.wireOp",EDGE,"E19.2.3"),sQuery(id+"F2.wireOp",EDGE,"E19.2.4"),sQuery(id+"F2.wireOp",EDGE,"E19.2.5"),sQuery(id+"F2.wireOp",EDGE,"E19.2.6"),sQuery(id+"F2.wireOp",EDGE,"E19.2.7"),sQuery(id+"F2.wireOp",EDGE,"E19.2.8"),sQuery(id+"F2.wireOp",EDGE,"E19.2.9")])],"isStart":true})]});}
            var Q19;
            Q19=makeQuery(id+"F3.opExtrude","CAP_EDGE",EDGE,{"disambiguationData":[OSD([sQuery(id+"F2.wireOp",EDGE,"E16.filletArc")])],"isStart":true});
            var Q20;
            Q20=makeQuery(id+"F3.opExtrude","CAP_EDGE",EDGE,{"disambiguationData":[OSD([sQuery(id+"F2.wireOp",EDGE,"E15.filletArc")])],"isStart":true});
            var Q21;
            Q21=makeQuery(id+"F3.opExtrude","CAP_EDGE",EDGE,{"disambiguationData":[OSD([sQuery(id+"F2.wireOp",EDGE,"E19.2.9")])],"isStart":true});
            chamfer(context, id + "F5", {"entities" : qUnion([Q0, Q1, Q2, Q3, Q4, Q5, Q6, Q7, Q8, Q9, Q10, Q11, Q12, Q13, Q14, Q15, Q16, Q17, Q18, Q19, Q20, Q21]), "width" : 2 * mm, "tangentPropagation" : true});
        }
        {
            var Q0;
            Q0=makeQuery(id+"F1.opExtrude","CAP_FACE",FACE,{"disambiguationData":[OSD([sQuery(id+"F0.wireOp",EDGE,"E0"),sQuery(id+"F0.wireOp",EDGE,"E1")])],"isStart":true});
            var sketch = newSketch(context, id + "F6", { "sketchPlane" : qUnion([Q0])});
            skCircle(sketch, "E20.0", {"center": v(0, 0) * mm, "radius": 10 * mm});
            skSolve(sketch);
        }
        {
            var Q0;
            Q0=makeQuery(id+"F6.imprint","IMPRINT",FACE,{"disambiguationData":[TD([[makeQuery(id+"F6.imprint","IMPRINT",EDGE,{"derivedFrom":sQuery(id+"F6.wireOp",EDGE,"E20.0")}),1.0]])]});
            var Q1;
            Q1=makeQuery(id+"F6.imprint","IMPRINT",FACE,{"disambiguationData":[TD([[makeQuery(id+"F6.imprint","IMPRINT",EDGE,{"derivedFrom":sQuery(id+"F6.wireOp",EDGE,"c407c948-2510-426a-b12c-06ac0bc9cf64.0")}),-1.0]])]});
            var Q2;
            Q2=makeQuery(id+"F6.imprint","IMPRINT",FACE,{"disambiguationData":[TD([[makeQuery(id+"F6.imprint","IMPRINT",EDGE,{"derivedFrom":sQuery(id+"F6.wireOp",EDGE,"c407c948-2510-426a-b12c-06ac0bc9cf64.0")}),1.0]])]});
            var Q3;
            Q3=makeQuery(id+"F6.imprint","IMPRINT",FACE,{"disambiguationData":[TD([[makeQuery(id+"F6.imprint","IMPRINT",EDGE,{"derivedFrom":makeQuery(id+"F1.opExtrude","CAP_EDGE",EDGE,{"disambiguationData":[OSD([sQuery(id+"F0.wireOp",EDGE,"E1")])],"isStart":true})}),-1.0]])]});
            extrude(context, id + "F7", {"entities" : qUnion([Q0, Q1, Q2, Q3]), "depth" : 2 * mm, "offsetDistance" : 25 * mm});
        }
        {
            var Q0;
            Q0=makeQuery(id+"F6.imprint","IMPRINT",FACE,{"disambiguationData":[TD([[makeQuery(id+"F6.imprint","IMPRINT",EDGE,{"derivedFrom":makeQuery(id+"F1.opExtrude","CAP_EDGE",EDGE,{"disambiguationData":[OSD([sQuery(id+"F0.wireOp",EDGE,"E1")])],"isStart":true})}),-1.0]])]});
            extrude(context, id + "F8", {"entities" : qUnion([Q0]), "operationType" : NewBodyOperationType.ADD, "oppositeDirection" : true, "depth" : 7.5 * mm, "offsetDistance" : 25 * mm});
        }
        {
            var Q0;
            Q0=makeQuery(id+"F8.opExtrude","CAP_FACE",FACE,{"disambiguationData":[OSD([sQuery(id+"F0.wireOp",EDGE,"E1")])],"isStart":false});
            var sketch = newSketch(context, id + "F9", { "sketchPlane" : qUnion([Q0])});
            skCircle(sketch, "E21.0", {"center": v(0, 0) * mm, "radius": 10 * mm});
            skCircle(sketch, "E22.0", {"center": v(0, 0) * mm, "radius": 2.5 * mm});
            skSolve(sketch);
        }
        {
            var Q0;
            Q0=makeQuery(id+"F9.imprint","IMPRINT",FACE,{"disambiguationData":[TD([[makeQuery(id+"F9.imprint","IMPRINT",EDGE,{"derivedFrom":sQuery(id+"F9.wireOp",EDGE,"E22.0")}),1.0]])]});
            extrude(context, id + "F10", {"entities" : qUnion([Q0]), "operationType" : NewBodyOperationType.REMOVE, "oppositeDirection" : true, "depth" : 4 * mm, "offsetDistance" : 25 * mm});
        }
        {
            var Q0;
            Q0=makeQuery(id+"F9.imprint","IMPRINT",FACE,{"disambiguationData":[TD([[makeQuery(id+"F9.imprint","IMPRINT",EDGE,{"derivedFrom":sQuery(id+"F9.wireOp",EDGE,"E21.0")}),1.0]])]});
            var Q1;
            Q1=makeQuery(id+"F9.imprint","IMPRINT",FACE,{"disambiguationData":[TD([[makeQuery(id+"F9.imprint","IMPRINT",EDGE,{"derivedFrom":sQuery(id+"F9.wireOp",EDGE,"a1f51509-8c7b-4646-a507-0ed3af852b90.0")}),-1.0]])]});
            var Q2;
            Q2=makeQuery(id+"F9.imprint","IMPRINT",FACE,{"disambiguationData":[TD([[makeQuery(id+"F9.imprint","IMPRINT",EDGE,{"derivedFrom":sQuery(id+"F9.wireOp",EDGE,"15deca98-b56f-4649-b585-fda4b9412a6e.0")}),1.0]])]});
            var Q3;
            Q3=makeQuery(id+"F9.imprint","IMPRINT",FACE,{"disambiguationData":[TD([[makeQuery(id+"F9.imprint","IMPRINT",EDGE,{"derivedFrom":sQuery(id+"F9.wireOp",EDGE,"a1f51509-8c7b-4646-a507-0ed3af852b90.0")}),1.0]])]});
            var Q4;
            Q4=makeQuery(id+"F9.imprint","IMPRINT",FACE,{"disambiguationData":[TD([[makeQuery(id+"F9.imprint","IMPRINT",EDGE,{"derivedFrom":sQuery(id+"F9.wireOp",EDGE,"E22.0")}),-1.0]])]});
            var Q5;
            Q5=makeQuery(id+"F9.imprint","IMPRINT",FACE,{"disambiguationData":[TD([[makeQuery(id+"F9.imprint","IMPRINT",EDGE,{"derivedFrom":sQuery(id+"F9.wireOp",EDGE,"E22.0")}),1.0]])]});
            extrude(context, id + "F11", {"entities" : qUnion([Q0, Q1, Q2, Q3, Q4, Q5]), "depth" : 2 * mm, "offsetDistance" : 25 * mm});
        }
        {
            var Q0;
            Q0=makeQuery(id+"F9.imprint","IMPRINT",FACE,{"disambiguationData":[TD([[makeQuery(id+"F9.imprint","IMPRINT",EDGE,{"derivedFrom":sQuery(id+"F9.wireOp",EDGE,"E22.0")}),1.0]])]});
            extrude(context, id + "F12", {"entities" : qUnion([Q0]), "operationType" : NewBodyOperationType.ADD, "oppositeDirection" : true, "depth" : 3.9 * mm, "offsetDistance" : 25 * mm});
        }
        {
            var Q0;
            Q0=makeQuery(id+"F7.opExtrude","CAP_FACE",FACE,{"disambiguationData":[OSD([sQuery(id+"F6.wireOp",EDGE,"E20.0")])],"isStart":false});
            var Q1;
            Q1=makeQuery(id+"F11.opExtrude","CAP_EDGE",EDGE,{"disambiguationData":[OSD([sQuery(id+"F9.wireOp",EDGE,"E21.0")])],"isStart":false});
            chamfer(context, id + "F13", {"entities" : qUnion([Q0, Q1]), "width" : 1 * mm, "tangentPropagation" : true});
        }
        {
            var Q0;
            Q0=makeQuery(id+"F1.opExtrude","CAP_FACE",FACE,{"disambiguationData":[OSD([sQuery(id+"F0.wireOp",EDGE,"E0"),sQuery(id+"F0.wireOp",EDGE,"E1")])],"isStart":true});
            var Q1;
            Q1=makeQuery(id+"F1.opExtrude","CAP_FACE",FACE,{"disambiguationData":[OSD([sQuery(id+"F0.wireOp",EDGE,"E0"),sQuery(id+"F0.wireOp",EDGE,"E1")])],"isStart":false});
            fillet(context, id + "F14", {"entities" : qUnion([Q0, Q1]), "radius" : .5 * mm, "tangentPropagation" : true, "allowEdgeOverflow" : false});
        }
    });
